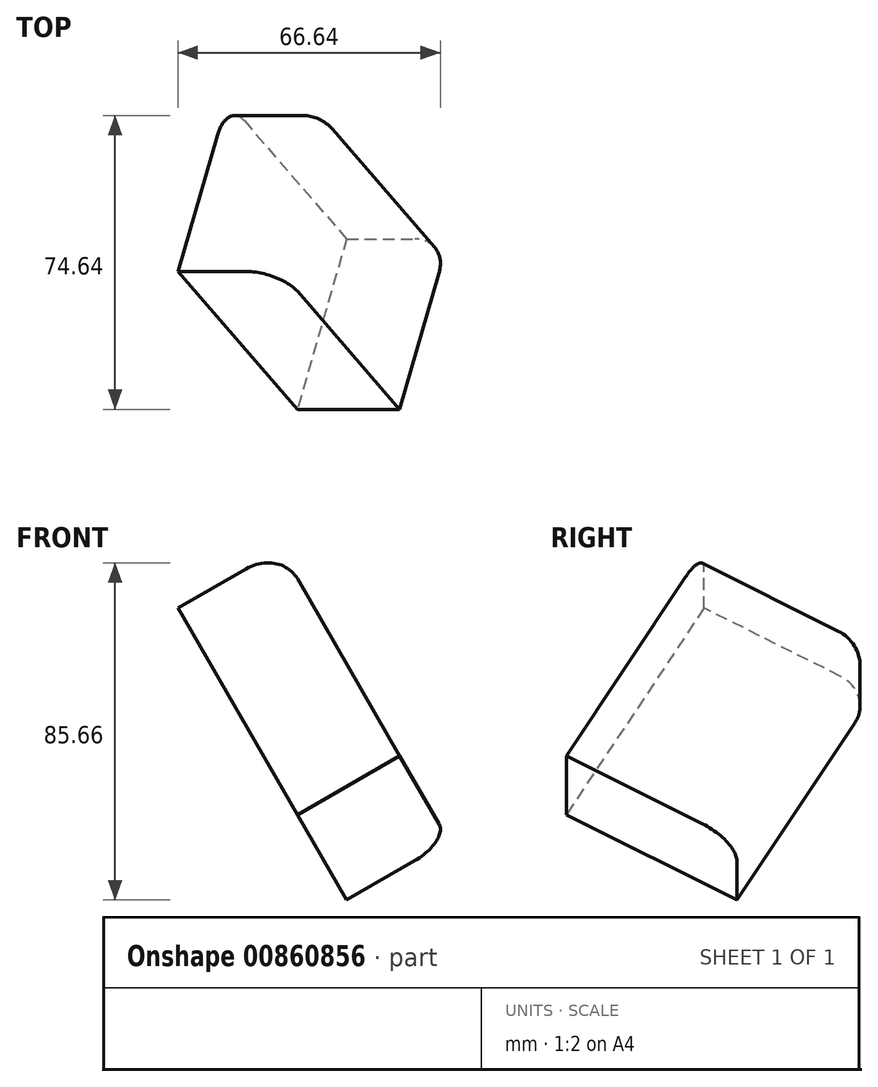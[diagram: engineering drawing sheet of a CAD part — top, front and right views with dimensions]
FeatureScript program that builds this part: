
annotation { "Feature Type Name" : "Feature", "Feature Type Description" : "" }
export const myFeature = defineFeature(function(context is Context, id is Id, definition is map)
    precondition{}
    {
        {
            var Q0;
            Q0=qCreatedBy(makeId("Top.planeOp"),FACE);
            var sketch = newSketch(context, id + "F0", { "sketchPlane" : qUnion([Q0])});
            skLineSegment(sketch, "E0.bottom", {"start": v(-15.08, 50) * mm, "end": v(14.92, 50) * mm});
            skLineSegment(sketch, "E0.top", {"start": v(-15.08, 0) * mm, "end": v(14.92, 0) * mm});
            skLineSegment(sketch, "E0.left", {"start": v(-15.08, 50) * mm, "end": v(-15.08, 0) * mm});
            skLineSegment(sketch, "E0.right", {"start": v(14.92, 50) * mm, "end": v(14.92, 0) * mm});
            skSolve(sketch);
        }
        {
            var Q0;
            Q0=makeQuery(id+"F0.imprint","IMPRINT",FACE,{"disambiguationData":[TD([[makeQuery(id+"F0.imprint","IMPRINT",EDGE,{"derivedFrom":sQuery(id+"F0.wireOp",EDGE,"E0.bottom")}),-1.0]])]});
            extrude(context, id + "F1", {"entities" : qUnion([Q0]), "depth" : 70 * mm, "offsetDistance" : 25 * mm});
        }
        {
            var Q0;
            Q0=makeQuery(id+"F1.opExtrude","SWEPT_BODY",BODY,{"disambiguationData":[OSD([sQuery(id+"F0.wireOp",EDGE,"E0.bottom"),sQuery(id+"F0.wireOp",EDGE,"E0.top"),sQuery(id+"F0.wireOp",EDGE,"E0.left"),sQuery(id+"F0.wireOp",EDGE,"E0.right")])]});
            transform(context, id + "F2", {"entities" : qUnion([Q0]), "transformType" : TransformType.TRANSLATION_3D, "dx" : 30 * mm, "dy" : 50 * mm, "dz" : 70 * mm, "makeCopy" : false});
        }
        {
            var Q0;
            Q0=makeQuery(id+"F1.opExtrude","CAP_EDGE",EDGE,{"disambiguationData":[OSD([sQuery(id+"F0.wireOp",EDGE,"E0.right")])],"isStart":false});
            var Q1;
            Q1=makeQuery(id+"F1.opExtrude","CAP_EDGE",EDGE,{"disambiguationData":[OSD([sQuery(id+"F0.wireOp",EDGE,"E0.bottom")])],"isStart":false});
            var Q2;
            Q2=makeQuery(id+"F1.opExtrude","SWEPT_EDGE",EDGE,{"disambiguationData":[OSD([sQuery(id+"F0.wireOp",EDGE,"E0.bottom"),sQuery(id+"F0.wireOp",EDGE,"E0.right")])]});
            fillet(context, id + "F3", {"entities" : qUnion([Q0, Q1, Q2]), "radius" : 10 * mm, "tangentPropagation" : true, "allowEdgeOverflow" : false});
        }
        {
            var Q0;
            Q0=makeQuery(id+"F1.opExtrude","SWEPT_BODY",BODY,{"disambiguationData":[OSD([sQuery(id+"F0.wireOp",EDGE,"E0.bottom"),sQuery(id+"F0.wireOp",EDGE,"E0.top"),sQuery(id+"F0.wireOp",EDGE,"E0.left"),sQuery(id+"F0.wireOp",EDGE,"E0.right")])]});
            var Q1;
            Q1=makeQuery(id+"F1.opExtrude","CAP_EDGE",EDGE,{"disambiguationData":[OSD([sQuery(id+"F0.wireOp",EDGE,"E0.left")])],"isStart":true});
            transform(context, id + "F4", {"entities" : qUnion([Q0]), "transformType" : TransformType.ROTATION, "transformAxis" : qUnion([Q1]), "angle" : 30 * degree, "makeCopy" : false});
        }
        {
            var Q0;
            Q0=makeQuery(id+"F1.opExtrude","SWEPT_BODY",BODY,{"disambiguationData":[OSD([sQuery(id+"F0.wireOp",EDGE,"E0.bottom"),sQuery(id+"F0.wireOp",EDGE,"E0.top"),sQuery(id+"F0.wireOp",EDGE,"E0.left"),sQuery(id+"F0.wireOp",EDGE,"E0.right")])]});
            var Q1;
            Q1=makeQuery(id+"F1.opExtrude","CAP_EDGE",EDGE,{"disambiguationData":[OSD([sQuery(id+"F0.wireOp",EDGE,"E0.bottom")])],"isStart":true});
            var Q2;
            Q2=makeQuery(id+"F1.opExtrude","CAP_EDGE",EDGE,{"disambiguationData":[OSD([sQuery(id+"F0.wireOp",EDGE,"E0.bottom")])],"isStart":true});
            transform(context, id + "F5", {"entities" : qUnion([Q0]), "transformType" : TransformType.ROTATION, "transformAxis" : qUnion([Q2]), "angle" : 30 * degree, "oppositeDirection" : true, "makeCopy" : false});
        }
    });
